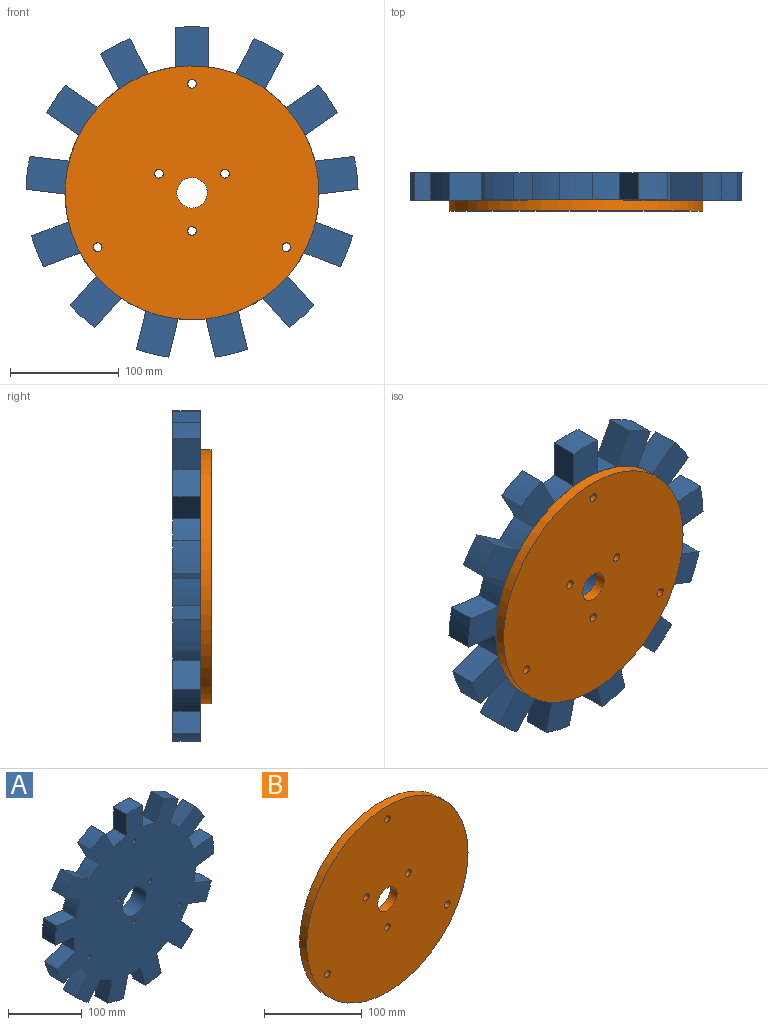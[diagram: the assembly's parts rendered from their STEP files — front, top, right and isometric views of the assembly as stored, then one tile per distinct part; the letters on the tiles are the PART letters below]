
ASSEMBLY  parts=2 mates=1
PART A: 61 faces, bbox 304.7x25x303.3 mm
  f0: plane 33.69x25mm, normal (-0.35,0,0.94), area 900.7mm2, adj f1,f58,f59,f60
  f1: cylinder r=152.4mm len=28.5mm, axis (0,1,0), area 763.3mm2, adj f0,f2,f59,f60
  f2: plane 33.69x25mm, normal (0.35,0,-0.94), area 900.7mm2, adj f1,f3,f59,f60
  f3: cylinder r=116.61mm len=25mm, axis (0,1,0), area 644.8mm2, adj f2,f4,f59,f60
  f4: plane 26.97x25mm, normal (-0.75,0,0.66), area 900.7mm2, adj f3,f5,f59,f60
  f5: cylinder r=152.4mm len=25mm, axis (0,1,0), area 763.3mm2, adj f4,f6,f59,f60
  f6: plane 26.97x25mm, normal (0.75,0,-0.66), area 900.7mm2, adj f5,f7,f59,f60
  f7: cylinder r=116.61mm len=25mm, axis (0,1,0), area 644.8mm2, adj f6,f8,f59,f60
  f8: plane 34.98x25mm, normal (-0.97,0,0.24), area 900.7mm2, adj f7,f9,f59,f60
  f9: cylinder r=152.4mm len=29.59mm, axis (0,1,0), area 763.3mm2, adj f8,f10,f59,f60
  f10: plane 34.98x25mm, normal (0.97,0,-0.24), area 900.7mm2, adj f9,f11,f59,f60
  f11: cylinder r=116.61mm len=25.74mm, axis (0,1,0), area 644.8mm2, adj f10,f12,f59,f60
  f12: plane 34.98x25mm, normal (-0.97,0,-0.24), area 900.7mm2, adj f11,f13,f59,f60
  f13: cylinder r=152.4mm len=29.59mm, axis (0,1,0), area 763.3mm2, adj f12,f14,f59,f60
  f14: plane 34.98x25mm, normal (0.97,0,0.24), area 900.7mm2, adj f13,f15,f59,f60
  f15: cylinder r=116.61mm len=25mm, axis (0,1,0), area 644.8mm2, adj f14,f16,f59,f60
  f16: plane 26.97x25mm, normal (-0.75,0,-0.66), area 900.7mm2, adj f15,f17,f59,f60
  f17: cylinder r=152.4mm len=25mm, axis (0,1,0), area 763.3mm2, adj f16,f18,f59,f60
  f18: plane 26.97x25mm, normal (0.75,0,0.66), area 900.7mm2, adj f17,f19,f59,f60
  f19: cylinder r=116.61mm len=25mm, axis (0,1,0), area 644.8mm2, adj f18,f20,f59,f60
  f20: plane 33.69x25mm, normal (-0.35,0,-0.94), area 900.7mm2, adj f19,f21,f59,f60
  f21: cylinder r=152.4mm len=28.5mm, axis (0,1,0), area 763.3mm2, adj f20,f22,f59,f60
  f22: plane 33.69x25mm, normal (0.35,0,0.94), area 900.7mm2, adj f21,f23,f59,f60
  f23: cylinder r=116.61mm len=25.55mm, axis (0,1,0), area 644.8mm2, adj f22,f24,f59,f60
  f24: plane 35.77x25mm, normal (0.12,0,-0.99), area 900.7mm2, adj f23,f25,f59,f60
  f25: cylinder r=152.4mm len=30.26mm, axis (0,1,0), area 763.3mm2, adj f24,f26,f59,f60
  f26: plane 35.77x25mm, normal (-0.12,0,0.99), area 900.7mm2, adj f25,f27,f59,f60
  f27: cylinder r=116.61mm len=25mm, axis (0,1,0), area 644.8mm2, adj f26,f28,f59,f60
  f28: plane 29.65x25mm, normal (0.57,0,-0.82), area 900.7mm2, adj f27,f29,f59,f60
  f29: cylinder r=152.4mm len=25.08mm, axis (0,1,0), area 763.3mm2, adj f28,f30,f59,f60
  f30: plane 29.65x25mm, normal (-0.57,0,0.82), area 900.7mm2, adj f29,f31,f59,f60
  f31: cylinder r=116.61mm len=25mm, axis (0,1,0), area 644.8mm2, adj f30,f32,f59,f60
  f32: plane 31.9x25mm, normal (0.89,0,-0.46), area 900.7mm2, adj f31,f33,f59,f60
  f33: cylinder r=152.4mm len=26.99mm, axis (0,1,0), area 763.3mm2, adj f32,f34,f59,f60
  f34: plane 31.9x25mm, normal (-0.89,0,0.46), area 900.7mm2, adj f33,f35,f59,f60
  f35: cylinder r=116.61mm len=25mm, axis (0,1,0), area 644.8mm2, adj f34,f36,f59,f60
  f36: plane 36.03x25mm, normal (1,0,0), area 900.7mm2, adj f35,f37,f59,f60
  f37: cylinder r=152.4mm len=30.48mm, axis (0,1,0), area 763.3mm2, adj f36,f38,f59,f60
  f38: plane 36.03x25mm, normal (-1,0,0), area 900.7mm2, adj f37,f39,f59,f60
  f39: cylinder r=116.61mm len=25mm, axis (0,1,0), area 644.8mm2, adj f38,f40,f59,f60
  f40: plane 31.9x25mm, normal (0.89,0,0.46), area 900.7mm2, adj f39,f41,f59,f60
  f41: cylinder r=152.4mm len=26.99mm, axis (0,1,0), area 763.3mm2, adj f40,f42,f59,f60
  f42: plane 31.9x25mm, normal (-0.89,0,-0.46), area 900.7mm2, adj f41,f43,f59,f60
  f43: cylinder r=116.61mm len=25mm, axis (0,1,0), area 644.8mm2, adj f42,f44,f59,f60
  f44: plane 29.65x25mm, normal (0.57,0,0.82), area 900.7mm2, adj f43,f45,f59,f60
  f45: cylinder r=152.4mm len=25.08mm, axis (0,1,0), area 763.3mm2, adj f44,f46,f59,f60
  f46: plane 29.65x25mm, normal (-0.57,0,-0.82), area 900.7mm2, adj f45,f47,f59,f60
  f47: cylinder r=116.61mm len=25mm, axis (0,1,0), area 644.8mm2, adj f46,f48,f59,f60
  f48: plane 35.77x25mm, normal (0.12,0,0.99), area 900.7mm2, adj f47,f49,f59,f60
  f49: cylinder r=152.4mm len=30.26mm, axis (0,1,0), area 763.3mm2, adj f48,f50,f59,f60
  f50: plane 35.77x25mm, normal (-0.12,0,-0.99), area 900.7mm2, adj f49,f58,f59,f60
  f51: cylinder r=22.61mm len=45.21mm, axis (0,1,0), area 3550.9mm2, adj f59,f60
  f52: cylinder r=4mm len=25mm, axis (0,1,0), area 628.3mm2, adj f59,f60
  f53: cylinder r=4mm len=25mm, axis (0,1,0), area 628.3mm2, adj f59,f60
  f54: cylinder r=4mm len=25mm, axis (0,1,0), area 628.3mm2, adj f59,f60
  f55: cylinder r=4mm len=25mm, axis (0,1,0), area 628.3mm2, adj f59,f60
  f56: cylinder r=4mm len=25mm, axis (0,1,0), area 628.3mm2, adj f59,f60
  f57: cylinder r=4mm len=25mm, axis (0,1,0), area 628.3mm2, adj f59,f60
  f58: cylinder r=116.61mm len=25.55mm, axis (0,1,0), area 644.8mm2, adj f0,f50,f59,f60
  f59: plane 304.74x303.28mm, normal (0,-1,0), area 55023.4mm2, adj f0,f1,f2,f3,f4,f5,f6,f7
  f60: plane 304.74x303.28mm, normal (0,1,0), area 55023.4mm2, adj f0,f1,f2,f3,f4,f5,f6,f7
PART B: 10 faces, bbox 233x10x233 mm
  f0: cylinder r=14mm len=28mm, axis (0,1,0), area 879.6mm2, adj f8,f9
  f1: cylinder r=4mm len=10mm, axis (0,1,0), area 251.3mm2, adj f8,f9
  f2: cylinder r=4mm len=10mm, axis (0,1,0), area 251.3mm2, adj f8,f9
  f3: cylinder r=4mm len=10mm, axis (0,1,0), area 251.3mm2, adj f8,f9
  f4: cylinder r=4mm len=10mm, axis (0,1,0), area 251.3mm2, adj f8,f9
  f5: cylinder r=4mm len=10mm, axis (0,1,0), area 251.3mm2, adj f8,f9
  f6: cylinder r=4mm len=10mm, axis (0,1,0), area 251.3mm2, adj f8,f9
  f7: cylinder r=116.5mm len=233mm, axis (0,1,0), area 7319.9mm2, adj f8,f9
  f8: plane 233x233mm, normal (0,-1,0), area 41721.1mm2, adj f0,f1,f2,f3,f4,f5,f6,f7
  f9: plane 233x233mm, normal (0,1,0), area 41721.1mm2, adj f0,f1,f2,f3,f4,f5,f6,f7
PLACE A rot(axis=(0.83,0.54,-0.1),0deg) t=(6.98,-96.55,44.94)mm
PLACE B rot(axis=(0.93,-0.36,-0.11),0deg) t=(6.98,-121.55,44.94)mm
MATE revolute A.f1 <-> B.f0  axis (0,-1,0) through (6.98,-121.55,44.94)mm
